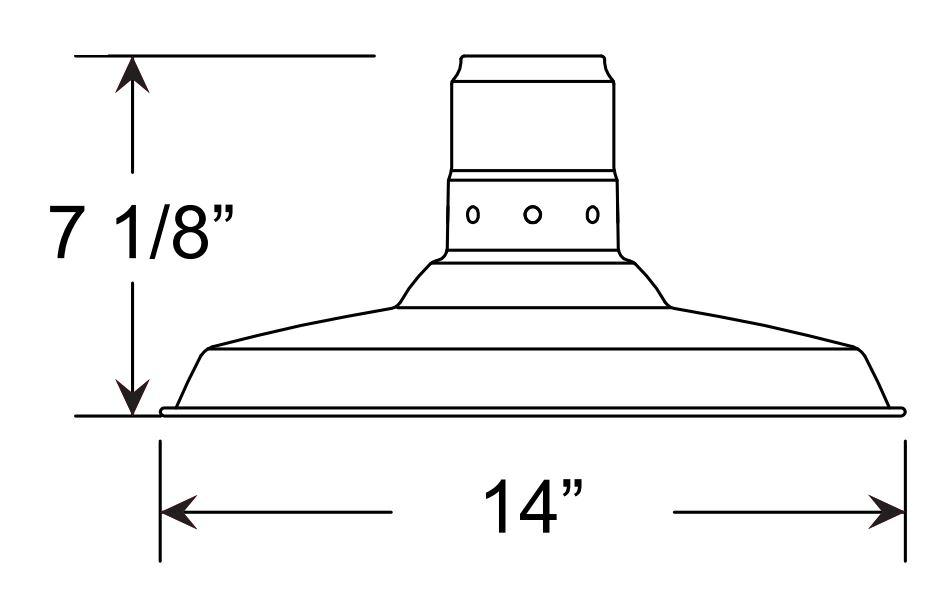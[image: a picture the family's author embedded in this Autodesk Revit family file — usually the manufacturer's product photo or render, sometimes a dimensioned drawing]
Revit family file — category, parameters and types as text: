
# Revit family: SPB MB
name_source: partatom
category: Lighting Fixtures
units: mm (PartAtom-declared; Revit-internal decimal feet)

## family parameters
Always vertical = Yes
Cut with Voids When Loaded = No
Light Source = Yes
OmniClass Number = 23.80.70.00
OmniClass Title = Lighting
Part Type = Normal
Room Calculation Point = No
Round Connector Dimension = Use Diameter
Shared = No
Work Plane-Based = No

## types (1)
- SPB
    Apparent Load = 60 VA
    Body Colour = Spun aluminium
    Body Material = body
    Color Filter = 16777215
    Construction Material = Heavy Duty spun aluminum.
    Default Elevation = 0' - 0"
    Description = 120-277 Voltage
    Dimming Lamp Color Temperature Shift = <None>
    Fixture Diameter = 0' - 1 1/2"
    Fixture Height = 0' - 3"
    GLASS = Glass
    Lamp = MED-BASE
    Load Classification = Lighting
    Manufacturer = ANP Lighting
    Model = SPB
    Photometric Web File = generic.ies
    Power Factor = 1
    Ring = RING
    SPB = Yes
    Tilt Angle = 90.00°
    URL = https://www.anplighting.com
    Voltage = 277 V
    Warranty = 5 year limited warranty
    Wattage Comments = 60W Max
    Weight = 0.30 lbs

## geometry (parser evidence)
native form markers: Sweep x24
no freeform markers — native parametric forms only
